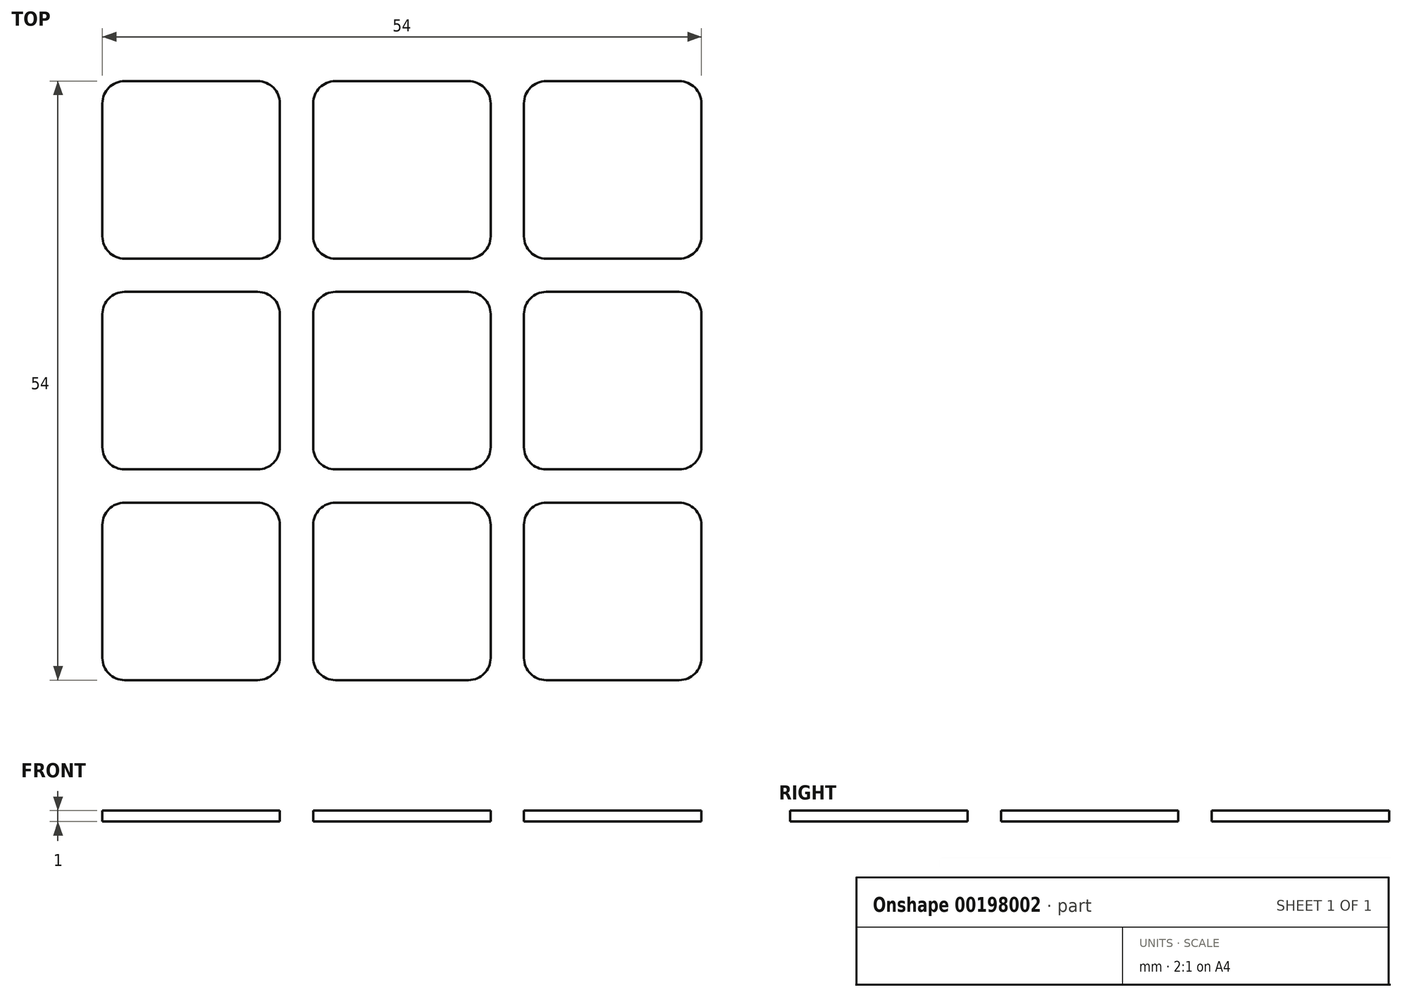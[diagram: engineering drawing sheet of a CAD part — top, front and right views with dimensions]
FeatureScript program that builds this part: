
annotation { "Feature Type Name" : "Feature", "Feature Type Description" : "" }
export const myFeature = defineFeature(function(context is Context, id is Id, definition is map)
    precondition{}
    {
        {
            var Q0;
            Q0=qCreatedBy(makeId("Top.planeOp"),FACE);
            var sketch = newSketch(context, id + "F0", { "sketchPlane" : qUnion([Q0])});
            skLineSegment(sketch, "E0.bottom", {"start": v(47.5, -9.5) * mm, "end": v(-9.5, -9.5) * mm, "construction": true});
            skLineSegment(sketch, "E0.top", {"start": v(47.5, 47.5) * mm, "end": v(-9.5, 47.5) * mm, "construction": true});
            skLineSegment(sketch, "E0.left", {"start": v(47.5, -9.5) * mm, "end": v(47.5, 47.5) * mm, "construction": true});
            skLineSegment(sketch, "E0.right", {"start": v(-9.5, -9.5) * mm, "end": v(-9.5, 47.5) * mm, "construction": true});
            skLineSegment(sketch, "E1", {"start": v(9.5, 47.5) * mm, "end": v(9.5, -9.5) * mm, "construction": true});
            skLineSegment(sketch, "E2", {"start": v(28.5, -9.5) * mm, "end": v(28.5, 47.5) * mm, "construction": true});
            skLineSegment(sketch, "E3", {"start": v(-9.5, 28.5) * mm, "end": v(47.5, 28.5) * mm, "construction": true});
            skLineSegment(sketch, "E4", {"start": v(47.5, 9.5) * mm, "end": v(-9.5, 9.5) * mm, "construction": true});
            skLineSegment(sketch, "E5.bottom", {"start": v(6, 8) * mm, "end": v(-6, 8) * mm});
            skLineSegment(sketch, "E5.top", {"start": v(6, -8) * mm, "end": v(-6, -8) * mm});
            skLineSegment(sketch, "E5.left", {"start": v(8, 6) * mm, "end": v(8, -6) * mm});
            skLineSegment(sketch, "E5.right", {"start": v(-8, 6) * mm, "end": v(-8, -6) * mm});
            skPoint(sketch, "E5.middle", {"position": v(0, 0) * mm});
            skPoint(sketch, "E6.visualSharp", {"position": v(-8, 8) * mm});
            skArc(sketch, "E6.filletArc", {"start": v(-6, 8) * mm, "mid": v(-7.41, 7.41) * mm, "end": v(-8, 6) * mm});
            skPoint(sketch, "E7.visualSharp", {"position": v(8, 8) * mm});
            skArc(sketch, "E7.filletArc", {"start": v(8, 6) * mm, "mid": v(7.41, 7.41) * mm, "end": v(6, 8) * mm});
            skPoint(sketch, "E8.visualSharp", {"position": v(8, -8) * mm});
            skArc(sketch, "E8.filletArc", {"start": v(6, -8) * mm, "mid": v(7.41, -7.41) * mm, "end": v(8, -6) * mm});
            skPoint(sketch, "E9.visualSharp", {"position": v(-8, -8) * mm});
            skArc(sketch, "E9.filletArc", {"start": v(-8, -6) * mm, "mid": v(-7.41, -7.41) * mm, "end": v(-6, -8) * mm});
            skArc(sketch, "E10.0.1.0", {"start": v(6, 11) * mm, "mid": v(7.41, 11.59) * mm, "end": v(8, 13) * mm});
            skLineSegment(sketch, "E10.0.1.1", {"start": v(6, 11) * mm, "end": v(-6, 11) * mm});
            skArc(sketch, "E10.0.1.2", {"start": v(-8, 13) * mm, "mid": v(-7.41, 11.59) * mm, "end": v(-6, 11) * mm});
            skLineSegment(sketch, "E10.0.1.3", {"start": v(-8, 25) * mm, "end": v(-8, 13) * mm});
            skArc(sketch, "E10.0.1.4", {"start": v(-6, 27) * mm, "mid": v(-7.41, 26.41) * mm, "end": v(-8, 25) * mm});
            skLineSegment(sketch, "E10.0.1.5", {"start": v(6, 27) * mm, "end": v(-6, 27) * mm});
            skArc(sketch, "E10.0.1.6", {"start": v(8, 25) * mm, "mid": v(7.41, 26.41) * mm, "end": v(6, 27) * mm});
            skLineSegment(sketch, "E10.0.1.7", {"start": v(8, 25) * mm, "end": v(8, 13) * mm});
            skArc(sketch, "E10.0.2.0", {"start": v(6, 30) * mm, "mid": v(7.41, 30.59) * mm, "end": v(8, 32) * mm});
            skLineSegment(sketch, "E10.0.2.1", {"start": v(6, 30) * mm, "end": v(-6, 30) * mm});
            skArc(sketch, "E10.0.2.2", {"start": v(-8, 32) * mm, "mid": v(-7.41, 30.59) * mm, "end": v(-6, 30) * mm});
            skLineSegment(sketch, "E10.0.2.3", {"start": v(-8, 44) * mm, "end": v(-8, 32) * mm});
            skArc(sketch, "E10.0.2.4", {"start": v(-6, 46) * mm, "mid": v(-7.41, 45.41) * mm, "end": v(-8, 44) * mm});
            skLineSegment(sketch, "E10.0.2.5", {"start": v(6, 46) * mm, "end": v(-6, 46) * mm});
            skArc(sketch, "E10.0.2.6", {"start": v(8, 44) * mm, "mid": v(7.41, 45.41) * mm, "end": v(6, 46) * mm});
            skLineSegment(sketch, "E10.0.2.7", {"start": v(8, 44) * mm, "end": v(8, 32) * mm});
            skArc(sketch, "E10.1.0.0", {"start": v(25, -8) * mm, "mid": v(26.41, -7.41) * mm, "end": v(27, -6) * mm});
            skLineSegment(sketch, "E10.1.0.1", {"start": v(25, -8) * mm, "end": v(13, -8) * mm});
            skArc(sketch, "E10.1.0.2", {"start": v(11, -6) * mm, "mid": v(11.59, -7.41) * mm, "end": v(13, -8) * mm});
            skLineSegment(sketch, "E10.1.0.3", {"start": v(11, 6) * mm, "end": v(11, -6) * mm});
            skArc(sketch, "E10.1.0.4", {"start": v(13, 8) * mm, "mid": v(11.59, 7.41) * mm, "end": v(11, 6) * mm});
            skLineSegment(sketch, "E10.1.0.5", {"start": v(25, 8) * mm, "end": v(13, 8) * mm});
            skArc(sketch, "E10.1.0.6", {"start": v(27, 6) * mm, "mid": v(26.41, 7.41) * mm, "end": v(25, 8) * mm});
            skLineSegment(sketch, "E10.1.0.7", {"start": v(27, 6) * mm, "end": v(27, -6) * mm});
            skArc(sketch, "E10.1.1.0", {"start": v(25, 11) * mm, "mid": v(26.41, 11.59) * mm, "end": v(27, 13) * mm});
            skLineSegment(sketch, "E10.1.1.1", {"start": v(25, 11) * mm, "end": v(13, 11) * mm});
            skArc(sketch, "E10.1.1.2", {"start": v(11, 13) * mm, "mid": v(11.59, 11.59) * mm, "end": v(13, 11) * mm});
            skLineSegment(sketch, "E10.1.1.3", {"start": v(11, 25) * mm, "end": v(11, 13) * mm});
            skArc(sketch, "E10.1.1.4", {"start": v(13, 27) * mm, "mid": v(11.59, 26.41) * mm, "end": v(11, 25) * mm});
            skLineSegment(sketch, "E10.1.1.5", {"start": v(25, 27) * mm, "end": v(13, 27) * mm});
            skArc(sketch, "E10.1.1.6", {"start": v(27, 25) * mm, "mid": v(26.41, 26.41) * mm, "end": v(25, 27) * mm});
            skLineSegment(sketch, "E10.1.1.7", {"start": v(27, 25) * mm, "end": v(27, 13) * mm});
            skArc(sketch, "E10.1.2.0", {"start": v(25, 30) * mm, "mid": v(26.41, 30.59) * mm, "end": v(27, 32) * mm});
            skLineSegment(sketch, "E10.1.2.1", {"start": v(25, 30) * mm, "end": v(13, 30) * mm});
            skArc(sketch, "E10.1.2.2", {"start": v(11, 32) * mm, "mid": v(11.59, 30.59) * mm, "end": v(13, 30) * mm});
            skLineSegment(sketch, "E10.1.2.3", {"start": v(11, 44) * mm, "end": v(11, 32) * mm});
            skArc(sketch, "E10.1.2.4", {"start": v(13, 46) * mm, "mid": v(11.59, 45.41) * mm, "end": v(11, 44) * mm});
            skLineSegment(sketch, "E10.1.2.5", {"start": v(25, 46) * mm, "end": v(13, 46) * mm});
            skArc(sketch, "E10.1.2.6", {"start": v(27, 44) * mm, "mid": v(26.41, 45.41) * mm, "end": v(25, 46) * mm});
            skLineSegment(sketch, "E10.1.2.7", {"start": v(27, 44) * mm, "end": v(27, 32) * mm});
            skArc(sketch, "E10.2.0.0", {"start": v(44, -8) * mm, "mid": v(45.41, -7.41) * mm, "end": v(46, -6) * mm});
            skLineSegment(sketch, "E10.2.0.1", {"start": v(44, -8) * mm, "end": v(32, -8) * mm});
            skArc(sketch, "E10.2.0.2", {"start": v(30, -6) * mm, "mid": v(30.59, -7.41) * mm, "end": v(32, -8) * mm});
            skLineSegment(sketch, "E10.2.0.3", {"start": v(30, 6) * mm, "end": v(30, -6) * mm});
            skArc(sketch, "E10.2.0.4", {"start": v(32, 8) * mm, "mid": v(30.59, 7.41) * mm, "end": v(30, 6) * mm});
            skLineSegment(sketch, "E10.2.0.5", {"start": v(44, 8) * mm, "end": v(32, 8) * mm});
            skArc(sketch, "E10.2.0.6", {"start": v(46, 6) * mm, "mid": v(45.41, 7.41) * mm, "end": v(44, 8) * mm});
            skLineSegment(sketch, "E10.2.0.7", {"start": v(46, 6) * mm, "end": v(46, -6) * mm});
            skArc(sketch, "E10.2.1.0", {"start": v(44, 11) * mm, "mid": v(45.41, 11.59) * mm, "end": v(46, 13) * mm});
            skLineSegment(sketch, "E10.2.1.1", {"start": v(44, 11) * mm, "end": v(32, 11) * mm});
            skArc(sketch, "E10.2.1.2", {"start": v(30, 13) * mm, "mid": v(30.59, 11.59) * mm, "end": v(32, 11) * mm});
            skLineSegment(sketch, "E10.2.1.3", {"start": v(30, 25) * mm, "end": v(30, 13) * mm});
            skArc(sketch, "E10.2.1.4", {"start": v(32, 27) * mm, "mid": v(30.59, 26.41) * mm, "end": v(30, 25) * mm});
            skLineSegment(sketch, "E10.2.1.5", {"start": v(44, 27) * mm, "end": v(32, 27) * mm});
            skArc(sketch, "E10.2.1.6", {"start": v(46, 25) * mm, "mid": v(45.41, 26.41) * mm, "end": v(44, 27) * mm});
            skLineSegment(sketch, "E10.2.1.7", {"start": v(46, 25) * mm, "end": v(46, 13) * mm});
            skArc(sketch, "E10.2.2.0", {"start": v(44, 30) * mm, "mid": v(45.41, 30.59) * mm, "end": v(46, 32) * mm});
            skLineSegment(sketch, "E10.2.2.1", {"start": v(44, 30) * mm, "end": v(32, 30) * mm});
            skArc(sketch, "E10.2.2.2", {"start": v(30, 32) * mm, "mid": v(30.59, 30.59) * mm, "end": v(32, 30) * mm});
            skLineSegment(sketch, "E10.2.2.3", {"start": v(30, 44) * mm, "end": v(30, 32) * mm});
            skArc(sketch, "E10.2.2.4", {"start": v(32, 46) * mm, "mid": v(30.59, 45.41) * mm, "end": v(30, 44) * mm});
            skLineSegment(sketch, "E10.2.2.5", {"start": v(44, 46) * mm, "end": v(32, 46) * mm});
            skArc(sketch, "E10.2.2.6", {"start": v(46, 44) * mm, "mid": v(45.41, 45.41) * mm, "end": v(44, 46) * mm});
            skLineSegment(sketch, "E10.2.2.7", {"start": v(46, 44) * mm, "end": v(46, 32) * mm});
            skLineSegment(sketch, "E10.direction1", {"start": v(-6, -8) * mm, "end": v(13, -8) * mm, "construction": true});
            skLineSegment(sketch, "E10.direction2", {"start": v(-6, -8) * mm, "end": v(-6, 11) * mm, "construction": true});
            skSolve(sketch);
        }
        {
            var Q0;
            Q0=qSketchRegion(id+"F0",true);
            extrude(context, id + "F1", {"entities" : qUnion([Q0]), "depth" : 1 * mm});
        }
    });
